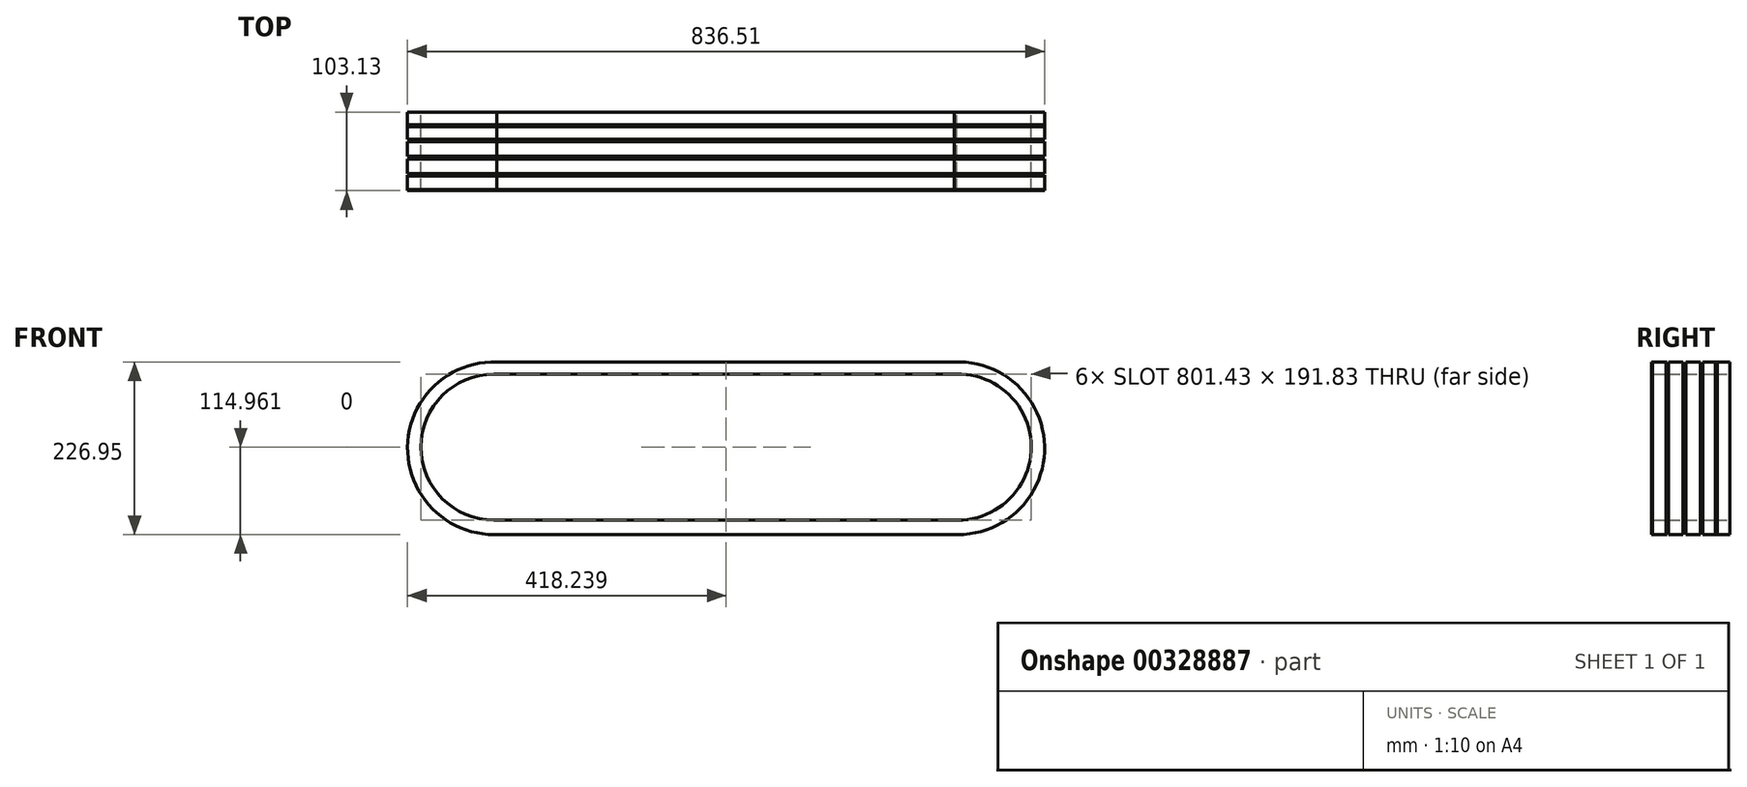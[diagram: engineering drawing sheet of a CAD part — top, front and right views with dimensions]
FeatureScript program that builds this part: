
annotation { "Feature Type Name" : "Feature", "Feature Type Description" : "" }
export const myFeature = defineFeature(function(context is Context, id is Id, definition is map)
    precondition{}
    {
        {
            var Q0;
            Q0=qCreatedBy(makeId("Front.planeOp"),FACE);
            var sketch = newSketch(context, id + "F0", { "sketchPlane" : qUnion([Q0])});
            skLineSegment(sketch, "E0", {"start": v(-301.27, 111.58) * mm, "end": v(299.47, 111.58) * mm});
            skLineSegment(sketch, "E1", {"start": v(-304.81, -115.24) * mm, "end": v(304.79, -115.24) * mm});
            skArc(sketch, "E2", {"start": v(-301.27, 111.58) * mm, "mid": v(-418.24, -0.03) * mm, "end": v(-304.81, -115.24) * mm});
            skArc(sketch, "E3", {"start": v(304.79, -115.24) * mm, "mid": v(418.23, 0.9) * mm, "end": v(299.47, 111.58) * mm});
            skLineSegment(sketch, "E4", {"start": v(-304.81, 95.64) * mm, "end": v(303.01, 95.64) * mm});
            skLineSegment(sketch, "E5", {"start": v(-304.81, -96.2) * mm, "end": v(304.79, -96.2) * mm});
            skArc(sketch, "E6", {"start": v(-304.81, 95.64) * mm, "mid": v(-400.73, -0.28) * mm, "end": v(-304.81, -96.2) * mm});
            skArc(sketch, "E7", {"start": v(304.79, -96.2) * mm, "mid": v(400.7, 0.61) * mm, "end": v(303.01, 95.64) * mm});
            skSolve(sketch);
        }
        {
            var Q0;
            Q0 = qSketchRegion(id + "F0", true);
            extrude(context, id + "F1", {"entities" : qUnion([Q0]), "depth" : 19.05 * mm});
        }
        {
            var Q0;
            Q0=makeQuery(id+"F1.opExtrude","SWEPT_BODY",BODY,{"disambiguationData":[OSD([sQuery(id+"F0.wireOp",EDGE,"E0"),sQuery(id+"F0.wireOp",EDGE,"E1"),sQuery(id+"F0.wireOp",EDGE,"E2"),sQuery(id+"F0.wireOp",EDGE,"E3"),sQuery(id+"F0.wireOp",EDGE,"E4"),sQuery(id+"F0.wireOp",EDGE,"E5"),sQuery(id+"F0.wireOp",EDGE,"E6"),sQuery(id+"F0.wireOp",EDGE,"E7")])]});
            transform(context, id + "F2", {"entities" : qUnion([Q0]), "transformType" : TransformType.TRANSLATION_3D, "dx" : 0 * mm, "dy" : 22.35 * mm, "dz" : 0 * mm, "makeCopy" : true});
        }
        {
            var Q0;
            Q0=makeQuery(id+"F2.opPattern","COPY",BODY,{"derivedFrom":makeQuery(id+"F1.opExtrude","SWEPT_BODY",BODY,{"disambiguationData":[OSD([sQuery(id+"F0.wireOp",EDGE,"E0"),sQuery(id+"F0.wireOp",EDGE,"E1"),sQuery(id+"F0.wireOp",EDGE,"E2"),sQuery(id+"F0.wireOp",EDGE,"E3"),sQuery(id+"F0.wireOp",EDGE,"E4"),sQuery(id+"F0.wireOp",EDGE,"E5"),sQuery(id+"F0.wireOp",EDGE,"E6"),sQuery(id+"F0.wireOp",EDGE,"E7")])]}),"instanceName":"1"});
            transform(context, id + "F3", {"entities" : qUnion([Q0]), "transformType" : TransformType.TRANSLATION_3D, "dx" : 0 * mm, "dy" : -44.96 * mm, "dz" : 0 * mm, "makeCopy" : true});
        }
        {
            var Q0;
            Q0=makeQuery(id+"F2.opPattern","COPY",BODY,{"derivedFrom":makeQuery(id+"F1.opExtrude","SWEPT_BODY",BODY,{"disambiguationData":[OSD([sQuery(id+"F0.wireOp",EDGE,"E0"),sQuery(id+"F0.wireOp",EDGE,"E1"),sQuery(id+"F0.wireOp",EDGE,"E2"),sQuery(id+"F0.wireOp",EDGE,"E3"),sQuery(id+"F0.wireOp",EDGE,"E4"),sQuery(id+"F0.wireOp",EDGE,"E5"),sQuery(id+"F0.wireOp",EDGE,"E6"),sQuery(id+"F0.wireOp",EDGE,"E7")])]}),"instanceName":"1"});
            transform(context, id + "F4", {"entities" : qUnion([Q0]), "transformType" : TransformType.TRANSLATION_3D, "dx" : 0 * mm, "dy" : -67.31 * mm, "dz" : 0 * mm, "makeCopy" : true});
        }
        {
            var Q0;
            Q0=makeQuery(id+"F1.opExtrude","SWEPT_BODY",BODY,{"disambiguationData":[OSD([sQuery(id+"F0.wireOp",EDGE,"E0"),sQuery(id+"F0.wireOp",EDGE,"E1"),sQuery(id+"F0.wireOp",EDGE,"E2"),sQuery(id+"F0.wireOp",EDGE,"E3"),sQuery(id+"F0.wireOp",EDGE,"E4"),sQuery(id+"F0.wireOp",EDGE,"E5"),sQuery(id+"F0.wireOp",EDGE,"E6"),sQuery(id+"F0.wireOp",EDGE,"E7")])]});
            transform(context, id + "F5", {"entities" : qUnion([Q0]), "transformType" : TransformType.TRANSLATION_3D, "dx" : 0 * mm, "dy" : -43.69 * mm, "dz" : 0 * mm, "makeCopy" : true});
        }
        {
            var Q0;
            Q0=makeQuery(id+"F1.opExtrude","SWEPT_BODY",BODY,{"disambiguationData":[OSD([sQuery(id+"F0.wireOp",EDGE,"E0"),sQuery(id+"F0.wireOp",EDGE,"E1"),sQuery(id+"F0.wireOp",EDGE,"E2"),sQuery(id+"F0.wireOp",EDGE,"E3"),sQuery(id+"F0.wireOp",EDGE,"E4"),sQuery(id+"F0.wireOp",EDGE,"E5"),sQuery(id+"F0.wireOp",EDGE,"E6"),sQuery(id+"F0.wireOp",EDGE,"E7")])]});
            transform(context, id + "F6", {"entities" : qUnion([Q0]), "transformType" : TransformType.TRANSLATION_3D, "dx" : 0 * mm, "dy" : 39.12 * mm, "dz" : 0 * mm, "makeCopy" : true});
        }
    });
